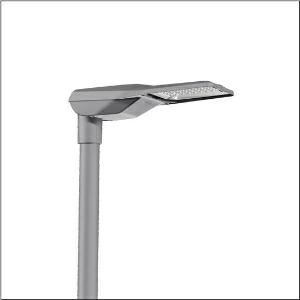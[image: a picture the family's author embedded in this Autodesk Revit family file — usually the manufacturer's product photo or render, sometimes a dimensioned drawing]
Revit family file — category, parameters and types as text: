
# Revit family: streetlight_sl_21_iq_mini___st0_8a_5xe2c31g08jb_bdc9
name_source: partatom
category: Lighting Fixtures
units: mm (PartAtom-declared; Revit-internal decimal feet)

## family parameters
Cut with Voids When Loaded = No
Host = Face
Light Source = No
Part Type = Normal
Room Calculation Point = No
Round Connector Dimension = Use Diameter
Shared = No

## types (1)
- --- (1 x LED, 10820 lm, 71.6 W, 3000K)
    Apparent Load = 72 VA
    CIE Flux Codes = 41 75 97 100 100
    Color Rendering = 70
    Color Temperature = 3000K
    Default Elevation = 1800 mm
    Description = Streetlight SL 21 iQ mini, mast luminaire, primary light control with lens, of PMMA, primary optical cover: cover, of toughened safety glass, transparent, light distribution: ST0.8a, light emission: direct distribution, primary light characteristic: asymmetric, installation type: post-top, side-entry, LED, High Power LED, rated luminous flux: 10.820lm, luminous efficacy: 151lm/W, light colour: 730, colour temperature: 3000K, control: Street-Remote, Auto-Match, Temp-Guard, Lumen-Switch, Night-Set, Smart-Wire, Light-Fading, Desk-Remote (wireless, voltage-free reading and setting of iQ features in the workshop via application-optimized NFC function/RFID function), optimised constant luminous flux control (CLO 2.0), presetting dimming linear, mains connection: 220..240V, AC, 50/60Hz, start of lifetime: 72W, end of service life: 75W, reduction: 33W, luminaire housing, of diecast aluminium, powder-coated, Siteco® metallic grey (DB 702S), corrosivity category C5 mid according to DIN EN ISO 12944, please order mast flange separately, inclination adjustable: 0°, 5°, 10°, 15°, sealing non-destructively replaceable, multi-level sealing system, length: 628mm, width: 235mm, height: 110mm, mast flange for spigot size: 42mm (side-entry): 5XC10008XM4, 60/48mm (side-entry/post-top): 5XC10108XM2, 76/60mm (side-entry/post-top): 5XC10108XM1, protection rating (complete): IP66, insulation class (complete): insulation class II (safety insulation), certification: CE, ENEC, ENEC+, VDE, impact resistance: IK09, permissible operating ambient temperature for outdoor applications: -40..+50°C, standard-compliant lighting for roads and squares, packaging unit: 1 piece

Light Distribution: ST0.8a
    Height = 110 mm
    Lamp = 1 x LED
    Lamp Light Flux = 10820 lm
    Lamp Power = 71.6 W
    Lamp count = 1
    Length = 625 mm
    Luminous efficacy = 151 lm/W
    Manufacturer = Siteco
    ModVariant = No
    Model = 5XE2C31G08JB
    Number of Poles = 1
    OnlyDefault = Yes
    Power Factor = 1
    Product Name = Streetlight SL 21 iQ mini | ST0.8a
    Product group = mast luminaire | pylon top
    ProductGroupID = 6100
    Protection Class = Protection class II
    Protection Degree = IP 66
    RLX_Detail_Level = 1
    RLX_Emergency_Light_Flux = 0 lm
    RLX_Emergency_Type = 0
    RLX_Emergency_Type_DB = No
    RlxData = <blob elided: 93741 chars, md5=c3e2aebb>
    Socket = socket
    Standby Power = 0 W
    System Light Flux = 10820 lm
    System Power = 72 W
    Type Comments = factory setting: luminous flux: 100 % | dim-lin: 254 | 746 mA
    Type Image = l_1003519.jpg
    URL = http://relux.com
    VarID = @adj_101849
    Voltage = 0 V
    Weight = 0.00 kg
    Width = 234 mm

## geometry (parser evidence)
native form markers: Blend x4, Sweep x12
no freeform markers — native parametric forms only
